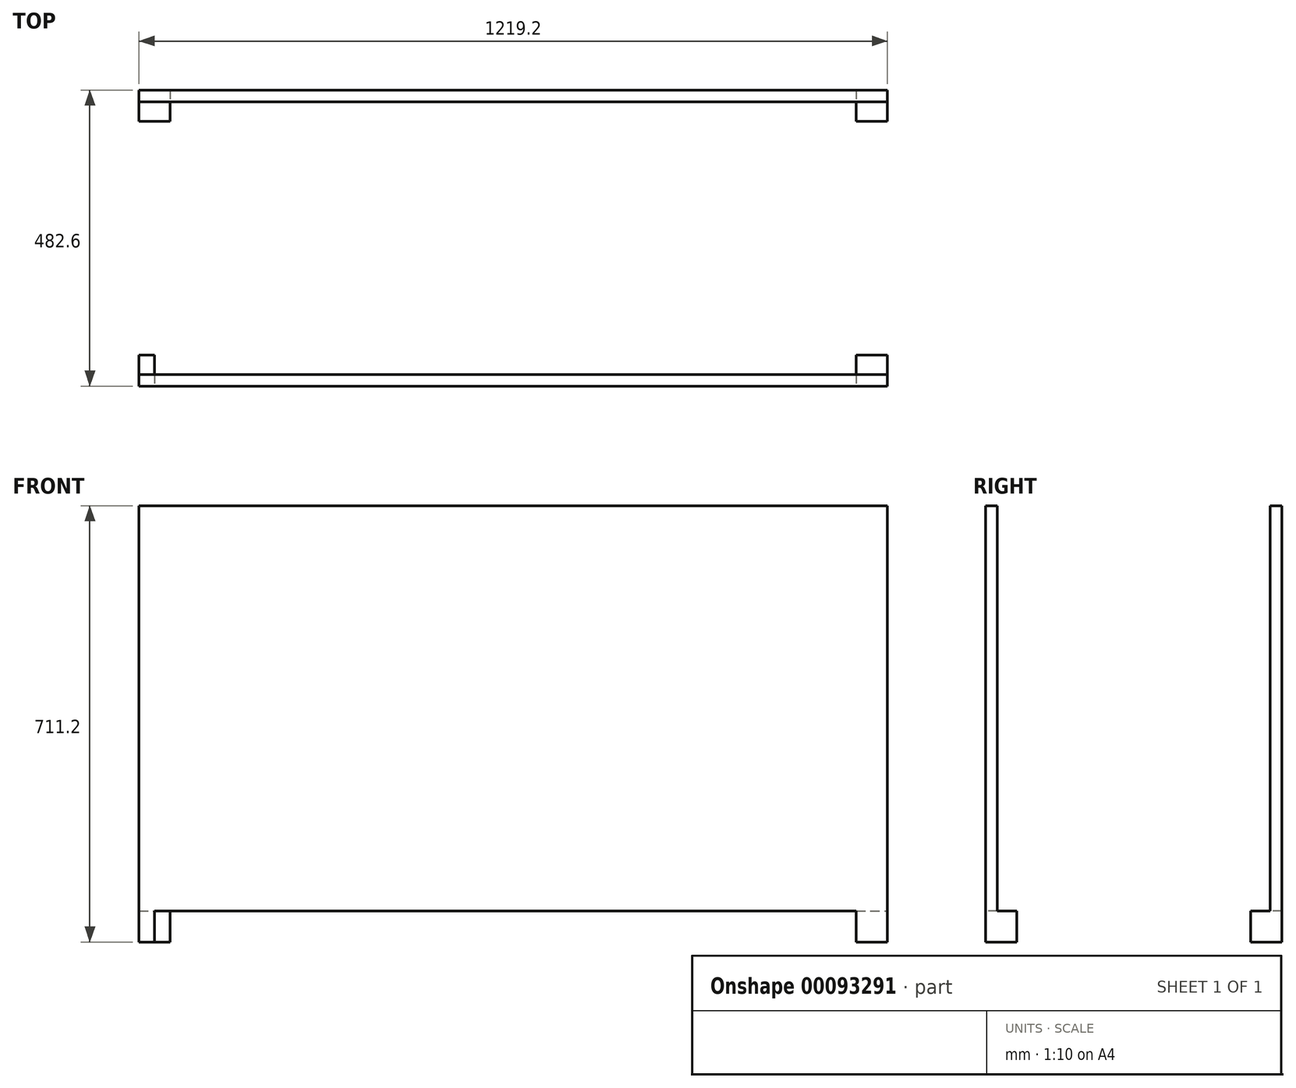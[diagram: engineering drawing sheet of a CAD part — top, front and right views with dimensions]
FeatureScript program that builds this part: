
annotation { "Feature Type Name" : "Feature", "Feature Type Description" : "" }
export const myFeature = defineFeature(function(context is Context, id is Id, definition is map)
    precondition{}
    {
        {
            var Q0;
            Q0=qCreatedBy(makeId("Front.planeOp"),FACE);
            var sketch = newSketch(context, id + "F0", { "sketchPlane" : qUnion([Q0])});
            skLineSegment(sketch, "E0.bottom", {"start": v(-589.85, 0) * mm, "end": v(629.35, 0) * mm});
            skLineSegment(sketch, "E0.top", {"start": v(-589.85, 711.2) * mm, "end": v(629.35, 711.2) * mm});
            skLineSegment(sketch, "E0.left", {"start": v(-589.85, 0) * mm, "end": v(-589.85, 711.2) * mm});
            skLineSegment(sketch, "E0.right", {"start": v(629.35, 0) * mm, "end": v(629.35, 711.2) * mm});
            skSolve(sketch);
        }
        {
            var Q0;
            Q0 = qSketchRegion(id + "F0", true);
            extrude(context, id + "F1", {"entities" : qUnion([Q0]), "oppositeDirection" : true, "depth" : 482.6 * mm});
        }
        {
            var Q0;
            Q0=makeQuery(id+"F1.opExtrude","CAP_FACE",FACE,{"disambiguationData":[OSD([sQuery(id+"F0.wireOp",EDGE,"E0.bottom"),sQuery(id+"F0.wireOp",EDGE,"E0.top"),sQuery(id+"F0.wireOp",EDGE,"E0.left"),sQuery(id+"F0.wireOp",EDGE,"E0.right")])],"isStart":true});
            var sketch = newSketch(context, id + "F2", { "sketchPlane" : qUnion([Q0])});
            skLineSegment(sketch, "E1.bottom", {"start": v(-589.85, 0) * mm, "end": v(-539.05, 0) * mm});
            skLineSegment(sketch, "E1.top", {"start": v(-589.85, 50.8) * mm, "end": v(-539.05, 50.8) * mm});
            skLineSegment(sketch, "E1.left", {"start": v(-589.85, 0) * mm, "end": v(-589.85, 50.8) * mm});
            skLineSegment(sketch, "E1.right", {"start": v(-539.05, 0) * mm, "end": v(-539.05, 50.8) * mm});
            skLineSegment(sketch, "E2.bottom", {"start": v(629.35, 0) * mm, "end": v(578.55, 0) * mm});
            skLineSegment(sketch, "E2.top", {"start": v(629.35, 50.8) * mm, "end": v(578.55, 50.8) * mm});
            skLineSegment(sketch, "E2.left", {"start": v(629.35, 0) * mm, "end": v(629.35, 50.8) * mm});
            skLineSegment(sketch, "E2.right", {"start": v(578.55, 0) * mm, "end": v(578.55, 50.8) * mm});
            skLineSegment(sketch, "E3.bottom", {"start": v(-539.05, 50.8) * mm, "end": v(578.55, 50.8) * mm});
            skLineSegment(sketch, "E3.top", {"start": v(-539.05, 0) * mm, "end": v(578.55, 0) * mm});
            skLineSegment(sketch, "E3.left", {"start": v(-539.05, 50.8) * mm, "end": v(-539.05, 0) * mm});
            skLineSegment(sketch, "E3.right", {"start": v(578.55, 50.8) * mm, "end": v(578.55, 0) * mm});
            skSolve(sketch);
        }
        {
            var Q0;
            Q0=makeQuery(id+"F2.imprint","IMPRINT",FACE,{"disambiguationData":[TD([[makeQuery(id+"F2.imprint","IMPRINT",EDGE,{"derivedFrom":sQuery(id+"F2.wireOp",EDGE,"E3.bottom")}),-1.0]])]});
            var Q1;
            Q1=makeQuery(id+"F1.opExtrude","CAP_FACE",FACE,{"disambiguationData":[OSD([sQuery(id+"F0.wireOp",EDGE,"E0.bottom"),sQuery(id+"F0.wireOp",EDGE,"E0.top"),sQuery(id+"F0.wireOp",EDGE,"E0.left"),sQuery(id+"F0.wireOp",EDGE,"E0.right")])],"isStart":false});
            extrude(context, id + "F3", {"entities" : qUnion([Q0]), "operationType" : NewBodyOperationType.REMOVE, "endBound" : BoundingType.UP_TO_SURFACE, "oppositeDirection" : true, "endBoundEntityFace" : qUnion([Q1]), "depth" : 25.4 * mm});
        }
        {
            var Q0;
            Q0=makeQuery(id+"F1.opExtrude","SWEPT_FACE",FACE,{"disambiguationData":[OSD([sQuery(id+"F0.wireOp",EDGE,"E0.right")])]});
            var sketch = newSketch(context, id + "F4", { "sketchPlane" : qUnion([Q0])});
            skLineSegment(sketch, "E4.bottom", {"start": v(0, 0) * mm, "end": v(50.8, 0) * mm});
            skLineSegment(sketch, "E4.top", {"start": v(0, 50.8) * mm, "end": v(50.8, 50.8) * mm});
            skLineSegment(sketch, "E4.left", {"start": v(0, 0) * mm, "end": v(0, 50.8) * mm});
            skLineSegment(sketch, "E4.right", {"start": v(50.8, 0) * mm, "end": v(50.8, 50.8) * mm});
            skLineSegment(sketch, "E5.bottom", {"start": v(482.6, 0) * mm, "end": v(431.8, 0) * mm});
            skLineSegment(sketch, "E5.top", {"start": v(482.6, 50.8) * mm, "end": v(431.8, 50.8) * mm});
            skLineSegment(sketch, "E5.left", {"start": v(482.6, 0) * mm, "end": v(482.6, 50.8) * mm});
            skLineSegment(sketch, "E5.right", {"start": v(431.8, 0) * mm, "end": v(431.8, 50.8) * mm});
            skLineSegment(sketch, "E6.bottom", {"start": v(50.8, 0) * mm, "end": v(431.8, 0) * mm});
            skLineSegment(sketch, "E6.top", {"start": v(50.8, 50.8) * mm, "end": v(431.8, 50.8) * mm});
            skSolve(sketch);
        }
        {
            var Q0;
            Q0=makeQuery(id+"F4.imprint","IMPRINT",FACE,{"disambiguationData":[TD([[makeQuery(id+"F4.imprint","IMPRINT",EDGE,{"derivedFrom":sQuery(id+"F4.wireOp",EDGE,"E6.bottom")}),-1.0]])]});
            var Q1;
            Q1=makeQuery(id+"F1.opExtrude","SWEPT_FACE",FACE,{"disambiguationData":[OSD([sQuery(id+"F0.wireOp",EDGE,"E0.left")])]});
            extrude(context, id + "F5", {"entities" : qUnion([Q0]), "operationType" : NewBodyOperationType.REMOVE, "endBound" : BoundingType.UP_TO_SURFACE, "oppositeDirection" : true, "endBoundEntityFace" : qUnion([Q1]), "depth" : 25.4 * mm});
        }
        {
            var Q0;
            Q0=makeQuery(id+"F1.opExtrude","SWEPT_FACE",FACE,{"disambiguationData":[OSD([sQuery(id+"F0.wireOp",EDGE,"E0.top")])]});
            var sketch = newSketch(context, id + "F6", { "sketchPlane" : qUnion([Q0])});
            skLineSegment(sketch, "E7.bottom", {"start": v(-589.85, 482.6) * mm, "end": v(-570.8, 482.6) * mm});
            skLineSegment(sketch, "E7.top", {"start": v(-589.85, 0) * mm, "end": v(-570.8, 0) * mm});
            skLineSegment(sketch, "E8.bottom", {"start": v(-589.85, 482.6) * mm, "end": v(629.35, 482.6) * mm});
            skLineSegment(sketch, "E8.top", {"start": v(-589.85, 463.55) * mm, "end": v(629.35, 463.55) * mm});
            skLineSegment(sketch, "E8.right", {"start": v(629.35, 482.6) * mm, "end": v(629.35, 463.55) * mm});
            skLineSegment(sketch, "E9.bottom", {"start": v(-589.85, 0) * mm, "end": v(629.35, 0) * mm});
            skLineSegment(sketch, "E9.top", {"start": v(-589.85, 19.05) * mm, "end": v(629.35, 19.05) * mm});
            skLineSegment(sketch, "E9.right", {"start": v(629.35, 0) * mm, "end": v(629.35, 19.05) * mm});
            skLineSegment(sketch, "E10.bottom", {"start": v(629.35, 463.55) * mm, "end": v(610.3, 463.55) * mm});
            skLineSegment(sketch, "E10.top", {"start": v(629.35, 19.05) * mm, "end": v(610.3, 19.05) * mm});
            skLineSegment(sketch, "E10.left", {"start": v(629.35, 463.55) * mm, "end": v(629.35, 19.05) * mm});
            skLineSegment(sketch, "E10.right", {"start": v(610.3, 463.55) * mm, "end": v(610.3, 19.05) * mm});
            skLineSegment(sketch, "E11.bottom", {"start": v(-589.85, 463.55) * mm, "end": v(-570.8, 463.55) * mm});
            skLineSegment(sketch, "E11.top", {"start": v(-589.85, 19.05) * mm, "end": v(-570.8, 19.05) * mm});
            skLineSegment(sketch, "E11.left", {"start": v(-589.85, 463.55) * mm, "end": v(-589.85, 19.05) * mm});
            skLineSegment(sketch, "E11.right", {"start": v(-570.8, 463.55) * mm, "end": v(-570.8, 19.05) * mm});
            skLineSegment(sketch, "E12", {"start": v(-570.8, 19.05) * mm, "end": v(-589.85, 19.05) * mm});
            skSolve(sketch);
        }
        {
            var Q0;
            Q0=makeQuery(id+"F6.imprint","IMPRINT",FACE,{"disambiguationData":[TD([[makeQuery(id+"F6.imprint","IMPRINT",EDGE,{"derivedFrom":sQuery(id+"F6.wireOp",EDGE,"E8.top")}),-1.0]])]});
            var Q1;
            Q1=makeQuery(id+"F5.boolean.opBoolean","MERGE",FACE,{"derivedFrom":[makeQuery(id+"F3.boolean.opBoolean","COPY",FACE,{"derivedFrom":makeQuery(id+"F3.opExtrude","SWEPT_FACE",FACE,{"disambiguationData":[OSD([sQuery(id+"F2.wireOp",EDGE,"E3.bottom")])]})}),makeQuery(id+"F5.opExtrude","SWEPT_FACE",FACE,{"disambiguationData":[OSD([sQuery(id+"F4.wireOp",EDGE,"E6.top")])]})]});
            extrude(context, id + "F7", {"entities" : qUnion([Q0]), "operationType" : NewBodyOperationType.REMOVE, "endBound" : BoundingType.UP_TO_SURFACE, "oppositeDirection" : true, "endBoundEntityFace" : qUnion([Q1]), "depth" : 25.4 * mm});
        }
        {
            var Q0;
            {var subQ1=sQuery(id+"F0.wireOp",EDGE,"E0.left");var subQ3=sQuery(id+"F0.wireOp",EDGE,"E0.bottom");var subQ5=makeQuery(id+"F1.opExtrude","SWEPT_FACE",FACE,{"disambiguationData":[OSD([subQ1])]});Q0=makeQuery(id+"F5.boolean.opBoolean","SPLIT",FACE,{"disambiguationData":[TD([makeQuery(id+"F5.opExtrude","SWEPT_FACE",FACE,{"disambiguationData":[OSD([sQuery(id+"F4.wireOp",EDGE,"E4.right")])]})])],"derivedFrom":makeQuery(id+"F3.boolean.opBoolean","SPLIT",FACE,{"disambiguationData":[TD([subQ5])],"derivedFrom":makeQuery(id+"F1.opExtrude","SWEPT_FACE",FACE,{"disambiguationData":[OSD([subQ3])]})})});}
            var sketch = newSketch(context, id + "F8", { "sketchPlane" : qUnion([Q0])});
            skLineSegment(sketch, "E13.bottom", {"start": v(-539.05, -50.8) * mm, "end": v(-564.45, -50.8) * mm});
            skLineSegment(sketch, "E13.top", {"start": v(-539.05, 0) * mm, "end": v(-564.45, 0) * mm});
            skLineSegment(sketch, "E13.left", {"start": v(-539.05, -50.8) * mm, "end": v(-539.05, 0) * mm});
            skLineSegment(sketch, "E13.right", {"start": v(-564.45, -50.8) * mm, "end": v(-564.45, 0) * mm});
            skSolve(sketch);
        }
        {
            var Q0;
            Q0=makeQuery(id+"F8.imprint","IMPRINT",FACE,{"disambiguationData":[TD([[makeQuery(id+"F8.imprint","IMPRINT",EDGE,{"derivedFrom":sQuery(id+"F8.wireOp",EDGE,"E13.bottom")}),1.0]])]});
            extrude(context, id + "F9", {"entities" : qUnion([Q0]), "operationType" : NewBodyOperationType.REMOVE, "oppositeDirection" : true, "depth" : 50.8 * mm});
        }
    });
